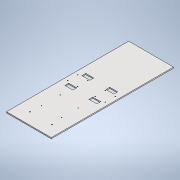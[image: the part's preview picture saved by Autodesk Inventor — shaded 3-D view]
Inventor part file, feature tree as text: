
AUTODESK INVENTOR PART (.ipt)
format: ipt  version: 2020 (Build 240168000, 168)  size: 150,528 bytes
history: native  units: mm
features: reference x14, other x8, extrude x4, sketch x4, mirror x1
ambient origin geometry x8: Origin, YZ Plane, XZ Plane, XY Plane, X Axis, Y Axis, Z Axis, Center Point
bodies: Body1 (feature_tree)
feature tree (31):
  other  "Твердое тело1"
  extrude  "Выдавливание1"  Depth=165.0mm
  extrude  "Выдавливание3"  Depth=450.0mm
  extrude  "Выдавливание4"  Depth=4.0mm TaperAngle=0.0deg
  extrude  "Выдавливание5"  Depth=4.0mm TaperAngle=0.0deg
  mirror  "Зеркальное отражение1"
  sketch  "Эскиз1"
  sketch  "Эскиз3"
  reference  "Ссылка1"
  reference  "Ссылка2"
  sketch  "Эскиз4"
  reference  "Ссылка3"
  reference  "Ссылка4"
  reference  "Ссылка5"
  reference  "Ссылка6"
  reference  "Ссылка7"
  reference  "Ссылка8"
  reference  "Ссылка9"
  reference  "Ссылка10"
  reference  "Ссылка11"
  reference  "Ссылка12"
  reference  "Ссылка13"
  reference  "Ссылка14"
  sketch  "Эскиз5"
  parser-record x1  (decoder bookkeeping rows leaked as tree rows — omitted from the tree; the rows remain in map.json)
  other  "test.iam"
  other  "realsenses_plate_v2.ipt:1"
  other  "realsenses_plate_2:2"
  other  "Odroid_n2:1"
  other  "L298N_V2:2"
  other  "L298N_V2:1"
note: 1 file-system path scrubbed to <path> (originals preserved in map.json)
